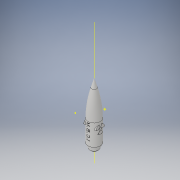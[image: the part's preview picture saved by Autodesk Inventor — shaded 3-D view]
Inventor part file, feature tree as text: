
AUTODESK INVENTOR PART (.ipt)
format: ipt  version: 2018 (Build 220112000, 112)  size: 635,904 bytes
history: native  units: in
note: dims shown in document units (in); Inventor stores cm internally (conversion verified against a paired STEP export)
features: other x5, sketch x4, plane x3, revolve x2, extrude x2, chamfer x2, hole x1, fillet x1
ambient origin geometry x8: Origin, YZ Plane, XZ Plane, XY Plane, X Axis, Y Axis, Z Axis, Center Point
bodies: Solid1 (feature_tree)
feature tree (20):
  sketch  "Sketch1"  dims[d3=90.0deg d42=1.0in]
  sketch  "Sketch2"  dims[d43=90.0deg]
  revolve  "Revolution2"  [1 undecoded]
  other  "Work Axis2"
  other  "Work Axis3"
  other  "Work Point2"
  revolve  "Revolution5"  [1 undecoded]
  other  "Work Point3"
  hole  "Hole4"  [1 undecoded]
  plane  "Work Plane9"
  extrude  "Extrusion3"  Depth=0.225in TaperAngle=45.0deg
  plane  "Work Plane10"
  fillet  "Fillet5"  Radius=0.225in
  extrude  "Extrusion4"  [1 undecoded]
  chamfer  "Chamfer1"  [1 undecoded]
  chamfer  "Chamfer2"  [1 undecoded]
  other  "Work Axis4"
  plane  "Work Plane8"
  sketch  "Sketch6"  dims[d58=1.0in d59=1.0in d47=0.4in d48=0.75in d49=0.375in d50=0.25in d51=0.5635in d52=1.5in d53=60.0deg d54=1.0in d55=0.0in]
  sketch  "Sketch7"  dims[d56=7.75in d57=1.0in d60=0.0in d61=0.225in d62=0.125in d63=45.0deg d64=0.225in d65=0.125in d66=45.0deg]
note: 6 required parameter values undecoded (feature->parameter linkage not recoverable at this tier; creation-order binding heuristic only, values carry confidence <= 0.55)